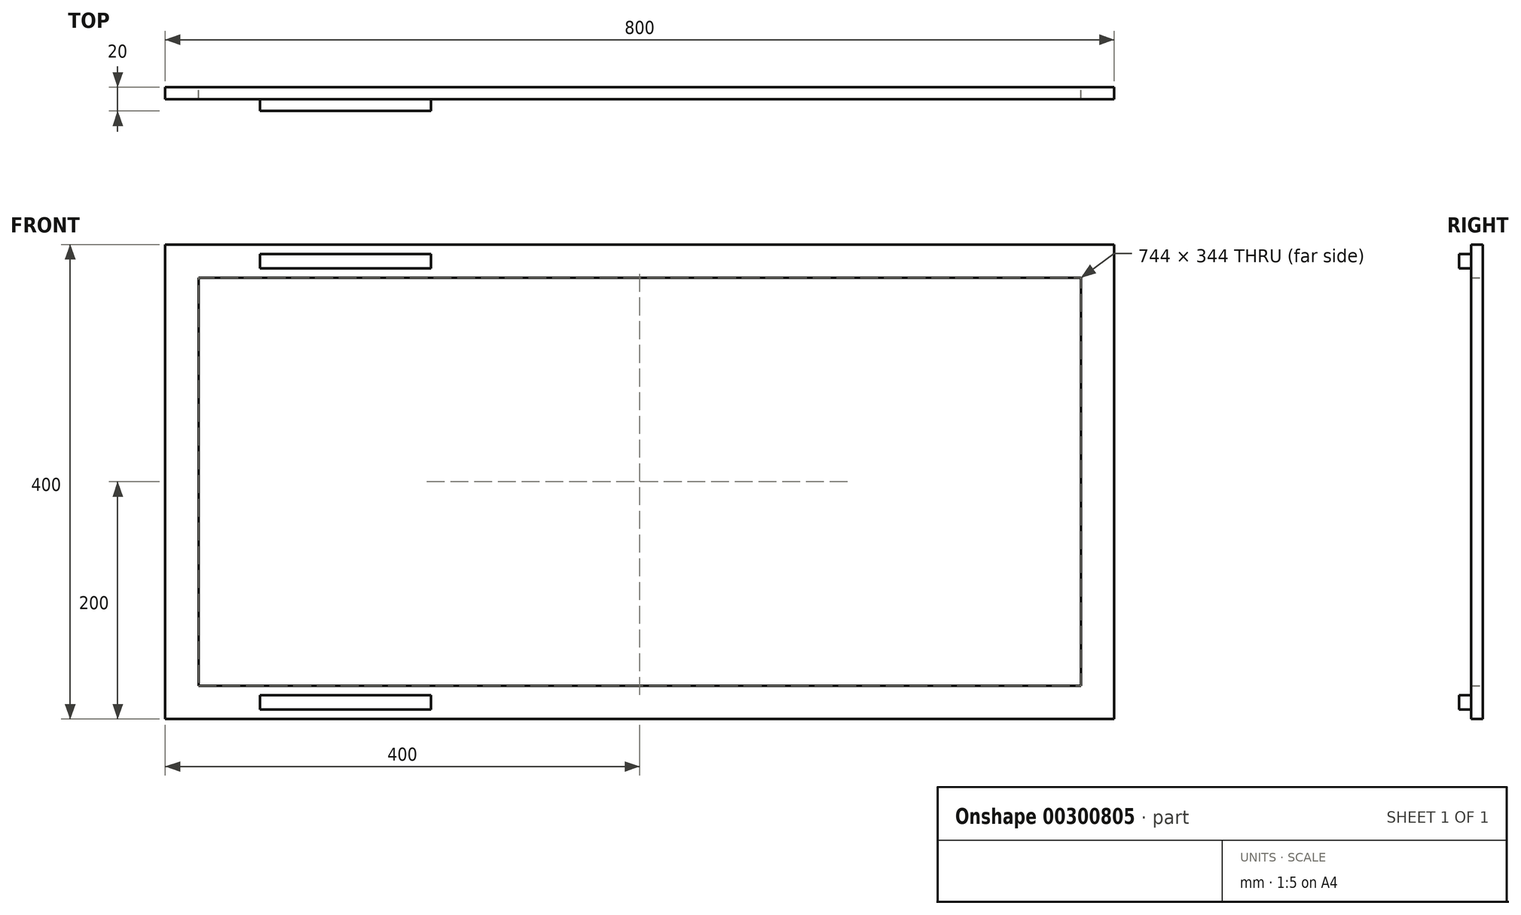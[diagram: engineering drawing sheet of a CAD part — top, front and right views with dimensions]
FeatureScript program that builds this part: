
annotation { "Feature Type Name" : "Feature", "Feature Type Description" : "" }
export const myFeature = defineFeature(function(context is Context, id is Id, definition is map)
    precondition{}
    {
        {
            var Q0;
            Q0=qCreatedBy(makeId("Front.planeOp"),FACE);
            var sketch = newSketch(context, id + "F0", { "sketchPlane" : qUnion([Q0])});
            skLineSegment(sketch, "E0.bottom", {"start": v(0, 0) * mm, "end": v(2000, 0) * mm});
            skLineSegment(sketch, "E0.top", {"start": v(0, -1000) * mm, "end": v(2000, -1000) * mm});
            skLineSegment(sketch, "E0.left", {"start": v(0, 0) * mm, "end": v(0, -1000) * mm});
            skLineSegment(sketch, "E0.right", {"start": v(2000, 0) * mm, "end": v(2000, -1000) * mm});
            skLineSegment(sketch, "E1.bottom", {"start": v(70, -70) * mm, "end": v(1930, -70) * mm});
            skLineSegment(sketch, "E1.top", {"start": v(70, -930) * mm, "end": v(1930, -930) * mm});
            skLineSegment(sketch, "E1.left", {"start": v(70, -70) * mm, "end": v(70, -930) * mm});
            skLineSegment(sketch, "E1.right", {"start": v(1930, -70) * mm, "end": v(1930, -930) * mm});
            skSolve(sketch);
        }
        {
            var Q0;
            Q0=makeQuery(id+"F0.imprint","IMPRINT",FACE,{"disambiguationData":[TD([[makeQuery(id+"F0.imprint","IMPRINT",EDGE,{"derivedFrom":sQuery(id+"F0.wireOp",EDGE,"E0.bottom")}),-1.0]])]});
            extrude(context, id + "F1", {"entities" : qUnion([Q0]), "depth" : 25 * mm});
        }
        {
            var Q0;
            Q0=makeQuery(id+"F1.opExtrude","CAP_FACE",FACE,{"disambiguationData":[OSD([sQuery(id+"F0.wireOp",EDGE,"E0.bottom"),sQuery(id+"F0.wireOp",EDGE,"E0.top"),sQuery(id+"F0.wireOp",EDGE,"E0.left"),sQuery(id+"F0.wireOp",EDGE,"E0.right"),sQuery(id+"F0.wireOp",EDGE,"E1.bottom"),sQuery(id+"F0.wireOp",EDGE,"E1.top"),sQuery(id+"F0.wireOp",EDGE,"E1.left"),sQuery(id+"F0.wireOp",EDGE,"E1.right")])],"isStart":false});
            var sketch = newSketch(context, id + "F2", { "sketchPlane" : qUnion([Q0])});
            skLineSegment(sketch, "E2.bottom", {"start": v(200, -20) * mm, "end": v(560, -20) * mm});
            skLineSegment(sketch, "E2.top", {"start": v(200, -50) * mm, "end": v(560, -50) * mm});
            skLineSegment(sketch, "E2.left", {"start": v(200, -20) * mm, "end": v(200, -50) * mm});
            skLineSegment(sketch, "E2.right", {"start": v(560, -20) * mm, "end": v(560, -50) * mm});
            skLineSegment(sketch, "E3.bottom", {"start": v(200, -950) * mm, "end": v(560, -950) * mm});
            skLineSegment(sketch, "E3.top", {"start": v(200, -980) * mm, "end": v(560, -980) * mm});
            skLineSegment(sketch, "E3.left", {"start": v(200, -950) * mm, "end": v(200, -980) * mm});
            skLineSegment(sketch, "E3.right", {"start": v(560, -950) * mm, "end": v(560, -980) * mm});
            skSolve(sketch);
        }
        {
            var Q0;
            Q0=makeQuery(id+"F2.imprint","IMPRINT",FACE,{"disambiguationData":[TD([[makeQuery(id+"F2.imprint","IMPRINT",EDGE,{"derivedFrom":sQuery(id+"F2.wireOp",EDGE,"E2.bottom")}),-1.0]])]});
            var Q1;
            Q1=makeQuery(id+"F2.imprint","IMPRINT",FACE,{"disambiguationData":[TD([[makeQuery(id+"F2.imprint","IMPRINT",EDGE,{"derivedFrom":sQuery(id+"F2.wireOp",EDGE,"E3.bottom")}),-1.0]])]});
            extrude(context, id + "F3", {"entities" : qUnion([Q0, Q1]), "operationType" : NewBodyOperationType.ADD, "depth" : 25 * mm});
        }
        {
            var Q0;
            Q0=makeQuery(id+"F1.opExtrude","SWEPT_BODY",BODY,{"disambiguationData":[OSD([sQuery(id+"F0.wireOp",EDGE,"E0.bottom"),sQuery(id+"F0.wireOp",EDGE,"E0.top"),sQuery(id+"F0.wireOp",EDGE,"E0.left"),sQuery(id+"F0.wireOp",EDGE,"E0.right"),sQuery(id+"F0.wireOp",EDGE,"E1.bottom"),sQuery(id+"F0.wireOp",EDGE,"E1.top"),sQuery(id+"F0.wireOp",EDGE,"E1.left"),sQuery(id+"F0.wireOp",EDGE,"E1.right")])]});
            var Q1;
            Q1=makeQuery(id+"F1.opExtrude","CAP_VERTEX",VERTEX,{"disambiguationData":[OSD([sQuery(id+"F0.wireOp",EDGE,"E0.top"),sQuery(id+"F0.wireOp",EDGE,"E0.right")])],"isStart":false});
            transform(context, id + "F4", {"entities" : qUnion([Q0]), "transformType" : TransformType.SCALE_UNIFORMLY, "scale" : 0.4, "scalePoint" : qUnion([Q1]), "makeCopy" : false});
        }
    });
